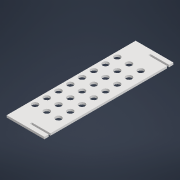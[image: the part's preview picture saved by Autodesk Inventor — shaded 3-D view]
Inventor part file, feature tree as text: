
AUTODESK INVENTOR PART (.ipt)
format: ipt  version: 2021.3 (Build 253353000, 353)  size: 306,176 bytes
history: native  units: in
note: dims shown in document units (in); Inventor stores cm internally (conversion verified against a paired STEP export)
features: extrude x1, sketch x1
ambient origin geometry x8: Origin, YZ Plane, XZ Plane, XY Plane, X Axis, Y Axis, Z Axis, Center Point
bodies: Solid1 (feature_tree)
feature tree (2):
  extrude  "Extrusion1"  Depth=15.2413in
  sketch  "Sketch1"  dims[d0=3.945in d1=15.2413in d7=0.7188in d8=1.75in d10=1.388in d11=1.388in d12=1.388in d13=1.388in d14=1.388in d15=1.388in d16=1.388in d17=1.388in d21=0.7188in d22=1.388in d23=1.388in d24=1.388in d25=1.388in d26=1.388in d27=1.388in d28=1.388in d31=0.25in d32=0.0in d34=0.7188in d35=1.388in d36=1.388in d37=1.388in d38=1.388in d39=1.388in d40=1.388in d41=1.388in d42=1.388in d48=0.23in d49=0.23in d50=2.0225in d51=0.5in d52=0.5in d53=6.9266in d54=0.05in]
